# Revit family: MT314
name_source: partatom
category: Apparecchi idraulici
units: mm (PartAtom-declared; Revit-internal decimal feet)

## family parameters
Basato su piano di lavoro = No
Condiviso = No
Mantieni orientamento annotazione = No
Numero OmniClass = 23.45.55.17
Punto di calcolo locali = No
Quota connettore circolare = Usa diametro
Sempre verticale = Sì
Taglio con vuoti quando caricato = No
Tipo di parte = Normale
Titolo OmniClass = Mixing Faucets

## types (13) — shared parameters
Cold water inlet = 10 mm  [stored 0.0328084 ft]
Commenti sul tipo = Wall mixer
Connessione CW = No
Connessione HW = No
Connessione di scarico = No
Connessione di ventilazione = No
Descrizione = Exposed parts for manual wall mixer with three ways diverter and shower kit
Hot water inlet = 10 mm  [stored 0.0328084 ft]
Produttore = IB Rubinetterie S.p.A.
URL = https://www.weareib.it
zero-valued in all types: Prospetto di default

## per-type parameters (varying)
| type | Finishes surface | Immagine tipo | Modello |
| Chrome | IB_Chrome | MT314CC.jpg | MT314CC |
| Brushed nickel | IB_Brushed nickel | MT314SS.jpg | MT314SS |
| Natural brass | IB_Brass | MT314ON.jpg | MT314ON |
| Matt white | IB_matt white | MT314BO.jpg | MT314BO |
| Matt black | IB_matt black | MT314NP.jpg | MT314NP |
| Black chrome | IB_Black chrome | MT314CF.jpg | MT314CF |
| Brushed black chrome | IB_Brushed black chrome | MT314CS.jpg | MT314CS |
| Pale gold | IB_Pale gold | MT314II.jpg | MT314II |
| Brushed pale gold | IB_brushed pale gold | MT314IS.jpg | MT314IS |
| Rose gold | IB_Rose gold | MT314RS.jpg | MT314RS |
| Brushed rose gold | IB_Brushed rose gold | MT314SR.jpg | MT314SR |
| Gold | IB_gold | MT314OO.jpg | MT314OO |
| Brushed gold | IB_brushed gold | MT314OS.jpg | MT314OS |

note: [stored X ft] marks values corroborated as IEEE doubles in the binary element streams (Revit-internal decimal feet)
